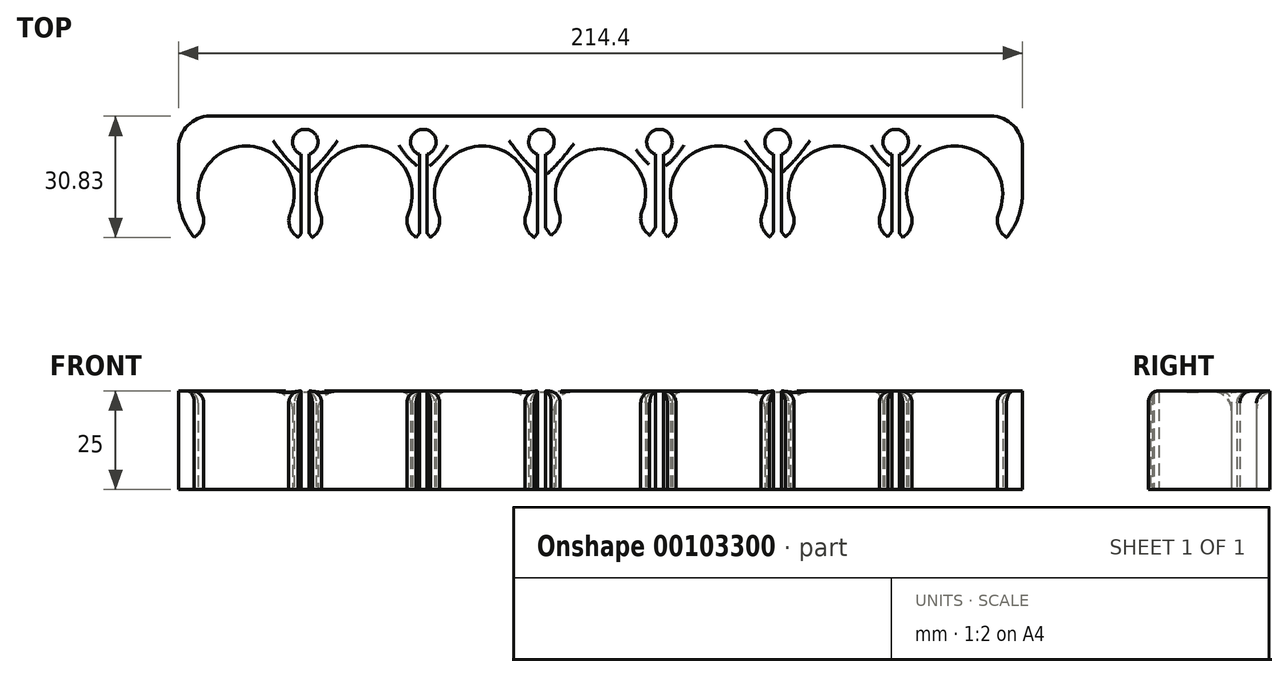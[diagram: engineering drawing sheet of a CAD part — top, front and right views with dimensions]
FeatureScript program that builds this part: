
annotation { "Feature Type Name" : "Feature", "Feature Type Description" : "" }
export const myFeature = defineFeature(function(context is Context, id is Id, definition is map)
    precondition{}
    {
        {
            var Q0;
            Q0=qCreatedBy(makeId("Top.planeOp"),FACE);
            var sketch = newSketch(context, id + "F0", { "sketchPlane" : qUnion([Q0])});
            skCircle(sketch, "E0", {"center": v(0, 0) * mm, "radius": 11.47 * mm});
            skLineSegment(sketch, "E1", {"start": v(0, 0) * mm, "end": v(30, 0) * mm, "construction": true});
            skLineSegment(sketch, "E2", {"start": v(30, 0) * mm, "end": v(60, 0) * mm, "construction": true});
            skLineSegment(sketch, "E3", {"start": v(60, 0) * mm, "end": v(90, 0) * mm, "construction": true});
            skLineSegment(sketch, "E4", {"start": v(0, 0) * mm, "end": v(-30, 0) * mm, "construction": true});
            skLineSegment(sketch, "E5", {"start": v(-30, 0) * mm, "end": v(-60, 0) * mm, "construction": true});
            skLineSegment(sketch, "E6", {"start": v(-60, 0) * mm, "end": v(-90, 0) * mm, "construction": true});
            skCircle(sketch, "E7", {"center": v(-90, 0) * mm, "radius": 12.2 * mm});
            skCircle(sketch, "E8", {"center": v(-60, 0) * mm, "radius": 12.2 * mm});
            skCircle(sketch, "E9", {"center": v(-30, 0) * mm, "radius": 12.2 * mm});
            skCircle(sketch, "E10", {"center": v(30, 0) * mm, "radius": 12.2 * mm});
            skCircle(sketch, "E11", {"center": v(60, 0) * mm, "radius": 12.2 * mm});
            skCircle(sketch, "E12", {"center": v(90, 0) * mm, "radius": 12.2 * mm});
            skArc(sketch, "E13.0", {"start": v(-107.2, 0) * mm, "mid": v(-95.25, -16.38) * mm, "end": v(-76, -10) * mm});
            skArc(sketch, "E14.0", {"start": v(-74, -10) * mm, "mid": v(-60, -17.2) * mm, "end": v(-46, -10) * mm});
            skArc(sketch, "E15.0", {"start": v(-44, -10) * mm, "mid": v(-30, -17.2) * mm, "end": v(-16, -10) * mm});
            skCircle(sketch, "E16.0", {"center": v(0, 0) * mm, "radius": 11.34 * mm});
            skArc(sketch, "E17.0", {"start": v(-14, -8.44) * mm, "mid": v(0, -16.34) * mm, "end": v(14, -8.44) * mm});
            skArc(sketch, "E18.0", {"start": v(76, -10) * mm, "mid": v(95.25, -16.38) * mm, "end": v(107.2, 0) * mm});
            skLineSegment(sketch, "E19", {"start": v(-107.2, 0) * mm, "end": v(-107.2, 11.77) * mm});
            skLineSegment(sketch, "E20", {"start": v(-99.2, 19.77) * mm, "end": v(99.2, 19.77) * mm});
            skLineSegment(sketch, "E21", {"start": v(107.2, 0) * mm, "end": v(107.2, 11.77) * mm});
            skArc(sketch, "E22.trimOffspring", {"start": v(46, -9.63) * mm, "mid": v(60, -16.84) * mm, "end": v(74, -9.63) * mm});
            skArc(sketch, "E23.trimOffspring", {"start": v(16, -9.63) * mm, "mid": v(30, -16.84) * mm, "end": v(44, -9.63) * mm});
            skPoint(sketch, "E24.visualSharp", {"position": v(-107.2, 19.77) * mm});
            skArc(sketch, "E24.filletArc", {"start": v(-99.2, 19.77) * mm, "mid": v(-104.86, 17.43) * mm, "end": v(-107.2, 11.77) * mm});
            skPoint(sketch, "E25.visualSharp", {"position": v(107.2, 19.77) * mm});
            skArc(sketch, "E25.filletArc", {"start": v(107.2, 11.77) * mm, "mid": v(104.86, 17.43) * mm, "end": v(99.2, 19.77) * mm});
            skArc(sketch, "E26", {"start": v(-74, 10.09) * mm, "mid": v(-75, 16.42) * mm, "end": v(-76, 10.09) * mm});
            skPoint(sketch, "E26.centerSnap0", {"position": v(-75, 0) * mm});
            skArc(sketch, "E27.1.0.0", {"start": v(-44, 10.09) * mm, "mid": v(-45, 16.42) * mm, "end": v(-46, 10.09) * mm});
            skArc(sketch, "E27.2.0.0", {"start": v(-14, 10.09) * mm, "mid": v(-15, 16.42) * mm, "end": v(-16, 10.09) * mm});
            skArc(sketch, "E27.3.0.0", {"start": v(16, 10.09) * mm, "mid": v(15, 16.42) * mm, "end": v(14, 10.09) * mm});
            skArc(sketch, "E27.4.0.0", {"start": v(46, 10.09) * mm, "mid": v(45, 16.42) * mm, "end": v(44, 10.09) * mm});
            skArc(sketch, "E27.5.0.0", {"start": v(76, 10.09) * mm, "mid": v(75, 16.42) * mm, "end": v(74, 10.09) * mm});
            skLineSegment(sketch, "E27.direction1", {"start": v(-75, 13.17) * mm, "end": v(-45, 13.17) * mm, "construction": true});
            skLineSegment(sketch, "E28", {"start": v(-90, 0) * mm, "end": v(-114.27, -20.36) * mm});
            skLineSegment(sketch, "E29", {"start": v(-90, 0) * mm, "end": v(-90, -30.2) * mm, "construction": true});
            skLineSegment(sketch, "E30", {"start": v(-90, 0) * mm, "end": v(-76, -11.75) * mm});
            skLineSegment(sketch, "E31.1.0.0", {"start": v(-60, 0) * mm, "end": v(-60, -30.2) * mm, "construction": true});
            skLineSegment(sketch, "E31.1.0.1", {"start": v(-60, 0) * mm, "end": v(-74, -11.75) * mm});
            skLineSegment(sketch, "E31.1.0.2", {"start": v(-60, 0) * mm, "end": v(-46, -11.75) * mm});
            skLineSegment(sketch, "E31.2.0.0", {"start": v(-30, 0) * mm, "end": v(-30, -30.2) * mm, "construction": true});
            skLineSegment(sketch, "E31.2.0.1", {"start": v(-30, 0) * mm, "end": v(-44, -11.75) * mm});
            skLineSegment(sketch, "E31.2.0.2", {"start": v(-30, 0) * mm, "end": v(-16, -11.75) * mm});
            skLineSegment(sketch, "E31.3.0.0", {"start": v(0, 0) * mm, "end": v(0, -30.2) * mm, "construction": true});
            skLineSegment(sketch, "E31.3.0.1", {"start": v(0, 0) * mm, "end": v(-14, -11.75) * mm});
            skLineSegment(sketch, "E31.3.0.2", {"start": v(0, 0) * mm, "end": v(14, -11.75) * mm});
            skLineSegment(sketch, "E31.4.0.0", {"start": v(30, 0) * mm, "end": v(30, -30.2) * mm, "construction": true});
            skLineSegment(sketch, "E31.4.0.1", {"start": v(30, 0) * mm, "end": v(16, -11.75) * mm});
            skLineSegment(sketch, "E31.4.0.2", {"start": v(30, 0) * mm, "end": v(44, -11.75) * mm});
            skLineSegment(sketch, "E31.5.0.0", {"start": v(60, 0) * mm, "end": v(60, -30.2) * mm, "construction": true});
            skLineSegment(sketch, "E31.5.0.1", {"start": v(60, 0) * mm, "end": v(46, -11.75) * mm});
            skLineSegment(sketch, "E31.5.0.2", {"start": v(60, 0) * mm, "end": v(74, -11.75) * mm});
            skLineSegment(sketch, "E31.6.0.0", {"start": v(90, 0) * mm, "end": v(90, -30.2) * mm, "construction": true});
            skLineSegment(sketch, "E31.6.0.1", {"start": v(90, 0) * mm, "end": v(76, -11.75) * mm});
            skLineSegment(sketch, "E31.6.0.2", {"start": v(90, 0) * mm, "end": v(112.58, -18.95) * mm});
            skLineSegment(sketch, "E31.direction1", {"start": v(-90, -30.2) * mm, "end": v(-60, -30.2) * mm, "construction": true});
            skLineSegment(sketch, "E32", {"start": v(-76, 10.09) * mm, "end": v(-76, -14.44) * mm});
            skLineSegment(sketch, "E33", {"start": v(-74, 10.09) * mm, "end": v(-74, -17.01) * mm});
            skLineSegment(sketch, "E34.1.0.0", {"start": v(-46, 13.17) * mm, "end": v(-46, -14.44) * mm});
            skLineSegment(sketch, "E34.1.0.1", {"start": v(-44, 13.17) * mm, "end": v(-44, -17.01) * mm});
            skLineSegment(sketch, "E34.2.0.0", {"start": v(-16, 13.17) * mm, "end": v(-16, -14.44) * mm});
            skLineSegment(sketch, "E34.2.0.1", {"start": v(-14, 13.17) * mm, "end": v(-14, -17.01) * mm});
            skLineSegment(sketch, "E34.3.0.0", {"start": v(14, 13.17) * mm, "end": v(14, -14.44) * mm});
            skLineSegment(sketch, "E34.3.0.1", {"start": v(16, 13.17) * mm, "end": v(16, -17.01) * mm});
            skLineSegment(sketch, "E34.4.0.0", {"start": v(44, 13.17) * mm, "end": v(44, -14.44) * mm});
            skLineSegment(sketch, "E34.4.0.1", {"start": v(46, 13.17) * mm, "end": v(46, -17.01) * mm});
            skLineSegment(sketch, "E34.5.0.0", {"start": v(74, 13.17) * mm, "end": v(74, -14.44) * mm});
            skLineSegment(sketch, "E34.5.0.1", {"start": v(76, 13.17) * mm, "end": v(76, -17.01) * mm});
            skLineSegment(sketch, "E34.direction1", {"start": v(-76, -14.44) * mm, "end": v(-46, -14.44) * mm, "construction": true});
            skPoint(sketch, "E35.orphan", {"position": v(-74, 13.17) * mm});
            skPoint(sketch, "E36.orphan", {"position": v(-76, 13.17) * mm});
            skLineSegment(sketch, "E37.trimOffspring", {"start": v(-76, -13.43) * mm, "end": v(-84.27, -20.36) * mm});
            skLineSegment(sketch, "E38.trimOffspring", {"start": v(-74, -13.43) * mm, "end": v(-67.42, -18.95) * mm});
            skLineSegment(sketch, "E39.trimOffspring", {"start": v(-46, -13.43) * mm, "end": v(-54.27, -20.36) * mm});
            skLineSegment(sketch, "E40.trimOffspring", {"start": v(-44, -13.43) * mm, "end": v(-37.42, -18.95) * mm});
            skLineSegment(sketch, "E41.trimOffspring", {"start": v(-14, -13.43) * mm, "end": v(-7.42, -18.95) * mm});
            skLineSegment(sketch, "E42.trimOffspring", {"start": v(-16, -13.43) * mm, "end": v(-24.27, -20.36) * mm});
            skLineSegment(sketch, "E43.trimOffspring", {"start": v(14, -13.43) * mm, "end": v(5.73, -20.36) * mm});
            skLineSegment(sketch, "E44.trimOffspring", {"start": v(16, -13.43) * mm, "end": v(22.58, -18.95) * mm});
            skLineSegment(sketch, "E45.trimOffspring", {"start": v(44, -13.43) * mm, "end": v(35.73, -20.36) * mm});
            skLineSegment(sketch, "E46.trimOffspring", {"start": v(46, -13.43) * mm, "end": v(52.58, -18.95) * mm});
            skLineSegment(sketch, "E47.trimOffspring", {"start": v(76, -13.43) * mm, "end": v(82.58, -18.95) * mm});
            skLineSegment(sketch, "E48.trimOffspring", {"start": v(74, -13.43) * mm, "end": v(65.73, -20.36) * mm});
            skSolve(sketch);
        }
        {
            var Q0;
            {var subQ13=sQuery(id+"F0.wireOp",EDGE,"E19");Q0=makeQuery(id+"F0.imprint","IMPRINT",FACE,{"disambiguationData":[TD([[makeQuery(id+"F0.imprint","IMPRINT",EDGE,{"derivedFrom":subQ13}),-1.0]])]});}
            extrude(context, id + "F1", {"entities" : qUnion([Q0]), "depth" : 25 * mm});
        }
        {
            var Q0;
            Q0=makeQuery(id+"F1.opExtrude","SWEPT_EDGE",EDGE,{"disambiguationData":[OSD([sQuery(id+"F0.wireOp",EDGE,"E12"),sQuery(id+"F0.wireOp",EDGE,"E31.6.0.2")])]});
            var Q1;
            Q1=makeQuery(id+"F1.opExtrude","SWEPT_EDGE",EDGE,{"disambiguationData":[OSD([sQuery(id+"F0.wireOp",EDGE,"E12"),sQuery(id+"F0.wireOp",EDGE,"E31.6.0.1")])]});
            var Q2;
            Q2=makeQuery(id+"F1.opExtrude","SWEPT_EDGE",EDGE,{"disambiguationData":[OSD([sQuery(id+"F0.wireOp",EDGE,"E11"),sQuery(id+"F0.wireOp",EDGE,"E31.5.0.2")])]});
            var Q3;
            Q3=makeQuery(id+"F1.opExtrude","SWEPT_EDGE",EDGE,{"disambiguationData":[OSD([sQuery(id+"F0.wireOp",EDGE,"E11"),sQuery(id+"F0.wireOp",EDGE,"E31.5.0.1")])]});
            var Q4;
            Q4=makeQuery(id+"F1.opExtrude","SWEPT_EDGE",EDGE,{"disambiguationData":[OSD([sQuery(id+"F0.wireOp",EDGE,"E10"),sQuery(id+"F0.wireOp",EDGE,"E31.4.0.2")])]});
            var Q5;
            Q5=makeQuery(id+"F1.opExtrude","SWEPT_EDGE",EDGE,{"disambiguationData":[OSD([sQuery(id+"F0.wireOp",EDGE,"E10"),sQuery(id+"F0.wireOp",EDGE,"E31.4.0.1")])]});
            var Q6;
            Q6=makeQuery(id+"F1.opExtrude","SWEPT_EDGE",EDGE,{"disambiguationData":[OSD([sQuery(id+"F0.wireOp",EDGE,"E0"),sQuery(id+"F0.wireOp",EDGE,"E31.3.0.2")])]});
            var Q7;
            Q7=makeQuery(id+"F1.opExtrude","SWEPT_EDGE",EDGE,{"disambiguationData":[OSD([sQuery(id+"F0.wireOp",EDGE,"E0"),sQuery(id+"F0.wireOp",EDGE,"E31.3.0.1")])]});
            var Q8;
            Q8=makeQuery(id+"F1.opExtrude","SWEPT_EDGE",EDGE,{"disambiguationData":[OSD([sQuery(id+"F0.wireOp",EDGE,"E9"),sQuery(id+"F0.wireOp",EDGE,"E31.2.0.2")])]});
            var Q9;
            Q9=makeQuery(id+"F1.opExtrude","SWEPT_EDGE",EDGE,{"disambiguationData":[OSD([sQuery(id+"F0.wireOp",EDGE,"E9"),sQuery(id+"F0.wireOp",EDGE,"E31.2.0.1")])]});
            var Q10;
            Q10=makeQuery(id+"F1.opExtrude","SWEPT_EDGE",EDGE,{"disambiguationData":[OSD([sQuery(id+"F0.wireOp",EDGE,"E8"),sQuery(id+"F0.wireOp",EDGE,"E31.1.0.2")])]});
            var Q11;
            Q11=makeQuery(id+"F1.opExtrude","SWEPT_EDGE",EDGE,{"disambiguationData":[OSD([sQuery(id+"F0.wireOp",EDGE,"E8"),sQuery(id+"F0.wireOp",EDGE,"E31.1.0.1")])]});
            var Q12;
            Q12=makeQuery(id+"F1.opExtrude","SWEPT_EDGE",EDGE,{"disambiguationData":[OSD([sQuery(id+"F0.wireOp",EDGE,"E7"),sQuery(id+"F0.wireOp",EDGE,"E30")])]});
            var Q13;
            Q13=makeQuery(id+"F1.opExtrude","SWEPT_EDGE",EDGE,{"disambiguationData":[OSD([sQuery(id+"F0.wireOp",EDGE,"E7"),sQuery(id+"F0.wireOp",EDGE,"E28")])]});
            fillet(context, id + "F2", {"entities" : qUnion([Q0, Q1, Q2, Q3, Q4, Q5, Q6, Q7, Q8, Q9, Q10, Q11, Q12, Q13]), "radius" : 5 * mm, "tangentPropagation" : true, "allowEdgeOverflow" : false});
        }
        {
            var Q0;
            Q0=makeQuery(id+"F1.opExtrude","CAP_EDGE",EDGE,{"disambiguationData":[OSD([sQuery(id+"F0.wireOp",EDGE,"E7")])],"isStart":false});
            var Q1;
            Q1=makeQuery(id+"F1.opExtrude","CAP_EDGE",EDGE,{"disambiguationData":[OSD([sQuery(id+"F0.wireOp",EDGE,"E8")])],"isStart":false});
            var Q2;
            Q2=makeQuery(id+"F1.opExtrude","CAP_EDGE",EDGE,{"disambiguationData":[OSD([sQuery(id+"F0.wireOp",EDGE,"E9")])],"isStart":false});
            var Q3;
            Q3=makeQuery(id+"F1.opExtrude","CAP_EDGE",EDGE,{"disambiguationData":[OSD([sQuery(id+"F0.wireOp",EDGE,"E27.1.0.0")])],"isStart":false});
            var Q4;
            Q4=makeQuery(id+"F1.opExtrude","CAP_EDGE",EDGE,{"disambiguationData":[OSD([sQuery(id+"F0.wireOp",EDGE,"E0")])],"isStart":false});
            var Q5;
            Q5=makeQuery(id+"F1.opExtrude","CAP_EDGE",EDGE,{"disambiguationData":[OSD([sQuery(id+"F0.wireOp",EDGE,"E10")])],"isStart":false});
            var Q6;
            Q6=makeQuery(id+"F1.opExtrude","CAP_EDGE",EDGE,{"disambiguationData":[OSD([sQuery(id+"F0.wireOp",EDGE,"E11")])],"isStart":false});
            var Q7;
            Q7=makeQuery(id+"F1.opExtrude","CAP_EDGE",EDGE,{"disambiguationData":[OSD([sQuery(id+"F0.wireOp",EDGE,"E12")])],"isStart":false});
            var Q8;
            Q8=makeQuery(id+"F1.opExtrude","CAP_EDGE",EDGE,{"disambiguationData":[OSD([sQuery(id+"F0.wireOp",EDGE,"E27.5.0.0")])],"isStart":false});
            var Q9;
            Q9=makeQuery(id+"F1.opExtrude","CAP_EDGE",EDGE,{"disambiguationData":[OSD([sQuery(id+"F0.wireOp",EDGE,"E27.3.0.0")])],"isStart":false});
            fillet(context, id + "F3", {"entities" : qUnion([Q0, Q1, Q2, Q3, Q4, Q5, Q6, Q7, Q8, Q9]), "radius" : 3 * mm, "tangentPropagation" : true, "allowEdgeOverflow" : false});
        }
        {
            var Q0;
            Q0=makeQuery(id+"F1.opExtrude","CAP_EDGE",EDGE,{"disambiguationData":[OSD([sQuery(id+"F0.wireOp",EDGE,"E26")])],"isStart":false});
            var Q1;
            Q1=makeQuery(id+"F1.opExtrude","CAP_EDGE",EDGE,{"disambiguationData":[OSD([sQuery(id+"F0.wireOp",EDGE,"E27.2.0.0")])],"isStart":false});
            var Q2;
            Q2=makeQuery(id+"F1.opExtrude","CAP_EDGE",EDGE,{"disambiguationData":[OSD([sQuery(id+"F0.wireOp",EDGE,"E27.4.0.0")])],"isStart":false});
            fillet(context, id + "F4", {"entities" : qUnion([Q0, Q1, Q2]), "radius" : 5 * mm, "tangentPropagation" : true, "allowEdgeOverflow" : false});
        }
    });
